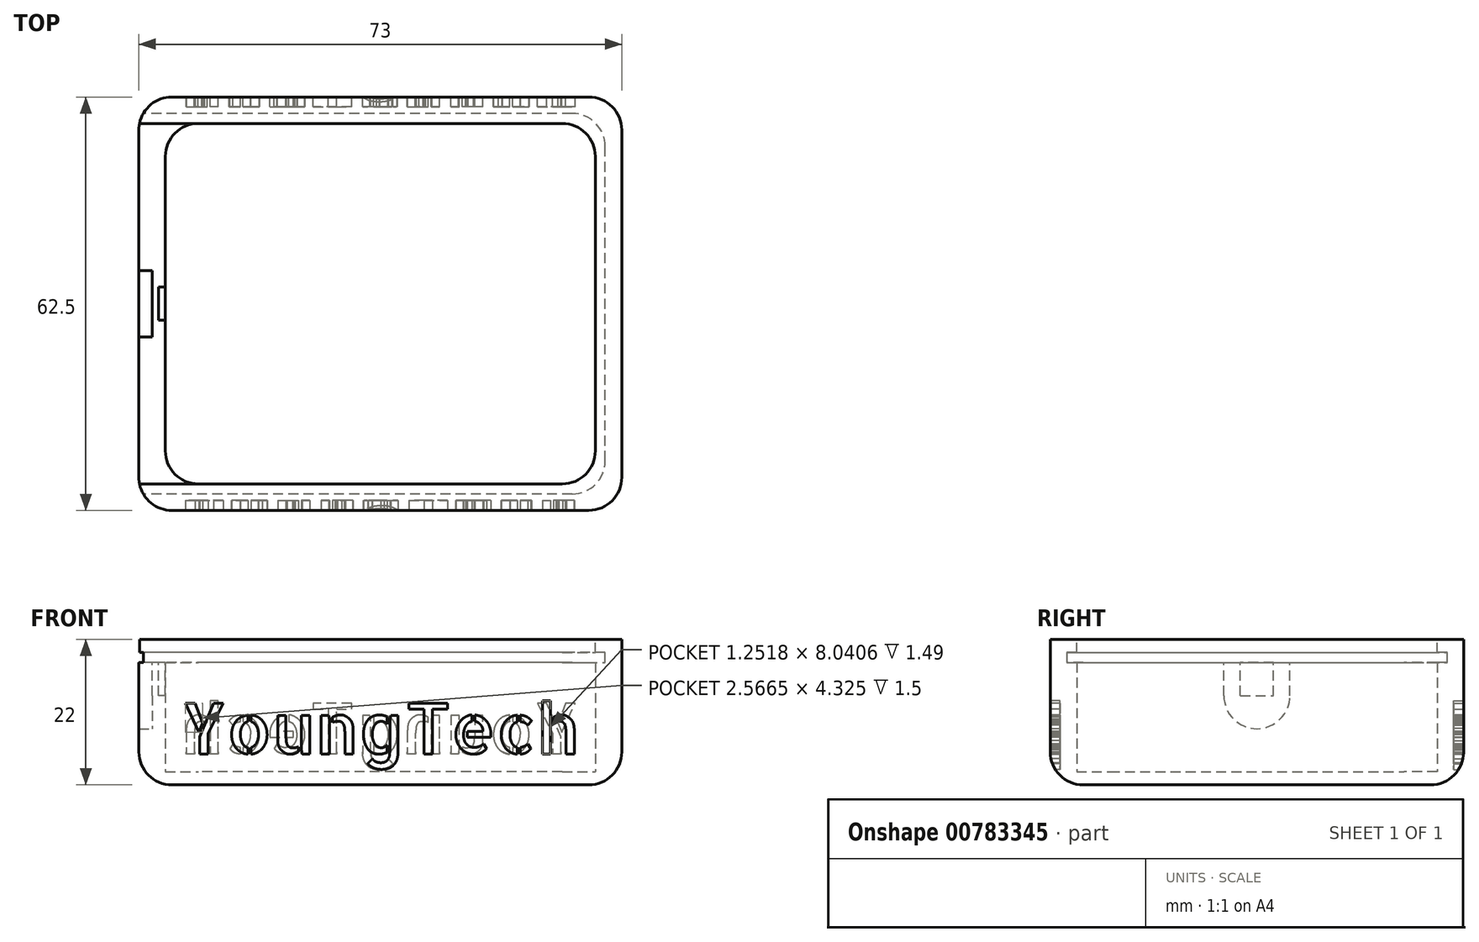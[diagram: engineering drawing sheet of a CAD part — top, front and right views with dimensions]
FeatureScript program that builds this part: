
annotation { "Feature Type Name" : "Feature", "Feature Type Description" : "" }
export const myFeature = defineFeature(function(context is Context, id is Id, definition is map)
    precondition{}
    {
        {
            var Q0;
            Q0=qCreatedBy(makeId("Top.planeOp"),FACE);
            var sketch = newSketch(context, id + "F0", { "sketchPlane" : qUnion([Q0])});
            skLineSegment(sketch, "E0.bottom", {"start": v(36.5, -31.25) * mm, "end": v(-36.5, -31.25) * mm});
            skLineSegment(sketch, "E0.top", {"start": v(36.5, 31.25) * mm, "end": v(-36.5, 31.25) * mm});
            skLineSegment(sketch, "E0.left", {"start": v(36.5, -31.25) * mm, "end": v(36.5, 31.25) * mm});
            skLineSegment(sketch, "E0.right", {"start": v(-36.5, -31.25) * mm, "end": v(-36.5, 31.25) * mm});
            skPoint(sketch, "E0.middle", {"position": v(0, 0) * mm});
            skSolve(sketch);
        }
        {
            var Q0;
            Q0=qSketchRegion(id+"F0",true);
            extrude(context, id + "F1", {"entities" : qUnion([Q0]), "depth" : 2 * mm, "offsetDistance" : 25 * mm});
        }
        {
            var Q0;
            Q0=makeQuery(id+"F1.opExtrude","CAP_FACE",FACE,{"disambiguationData":[OSD([sQuery(id+"F0.wireOp",EDGE,"E0.bottom"),sQuery(id+"F0.wireOp",EDGE,"E0.top"),sQuery(id+"F0.wireOp",EDGE,"E0.left"),sQuery(id+"F0.wireOp",EDGE,"E0.right")])],"isStart":false});
            var sketch = newSketch(context, id + "F2", { "sketchPlane" : qUnion([Q0])});
            skLineSegment(sketch, "E1.0.0", {"start": v(36.5, 31.25) * mm, "end": v(36.5, -31.25) * mm});
            skLineSegment(sketch, "E1.0.1", {"start": v(36.5, -31.25) * mm, "end": v(-36.5, -31.25) * mm});
            skLineSegment(sketch, "E1.0.2", {"start": v(-36.5, -31.25) * mm, "end": v(-36.5, 31.25) * mm});
            skLineSegment(sketch, "E1.0.3", {"start": v(-36.5, 31.25) * mm, "end": v(36.5, 31.25) * mm});
            skLineSegment(sketch, "E2.bottom", {"start": v(32.5, -27.25) * mm, "end": v(-32.5, -27.25) * mm});
            skLineSegment(sketch, "E2.top", {"start": v(32.5, 27.25) * mm, "end": v(-32.5, 27.25) * mm});
            skLineSegment(sketch, "E2.left", {"start": v(32.5, -27.25) * mm, "end": v(32.5, 27.25) * mm});
            skLineSegment(sketch, "E2.right", {"start": v(-32.5, -27.25) * mm, "end": v(-32.5, 27.25) * mm});
            skPoint(sketch, "E2.middle", {"position": v(0, 0) * mm});
            skSolve(sketch);
        }
        {
            var Q0;
            Q0=makeQuery(id+"F2.imprint","IMPRINT",FACE,{"disambiguationData":[TD([[makeQuery(id+"F2.imprint","IMPRINT",EDGE,{"derivedFrom":sQuery(id+"F2.wireOp",EDGE,"E1.0.0")}),1.0]])]});
            extrude(context, id + "F3", {"entities" : qUnion([Q0]), "operationType" : NewBodyOperationType.ADD, "depth" : 20 * mm, "offsetDistance" : 25 * mm});
        }
        {
            var Q0;
            Q0=makeQuery(id+"F3.boolean.opBoolean","MERGE",EDGE,{"derivedFrom":[makeQuery(id+"F1.opExtrude","SWEPT_EDGE",EDGE,{"disambiguationData":[OSD([sQuery(id+"F0.wireOp",EDGE,"E0.top"),sQuery(id+"F0.wireOp",EDGE,"E0.right")])]}),makeQuery(id+"F3.opExtrude","SWEPT_EDGE",EDGE,{"disambiguationData":[OSD([sQuery(id+"F2.wireOp",EDGE,"E1.0.2"),sQuery(id+"F2.wireOp",EDGE,"E1.0.3")])]})]});
            var Q1;
            Q1=makeQuery(id+"F3.boolean.opBoolean","MERGE",EDGE,{"derivedFrom":[makeQuery(id+"F1.opExtrude","SWEPT_EDGE",EDGE,{"disambiguationData":[OSD([sQuery(id+"F0.wireOp",EDGE,"E0.bottom"),sQuery(id+"F0.wireOp",EDGE,"E0.right")])]}),makeQuery(id+"F3.opExtrude","SWEPT_EDGE",EDGE,{"disambiguationData":[OSD([sQuery(id+"F2.wireOp",EDGE,"E1.0.1"),sQuery(id+"F2.wireOp",EDGE,"E1.0.2")])]})]});
            var Q2;
            Q2=makeQuery(id+"F3.boolean.opBoolean","MERGE",EDGE,{"derivedFrom":[makeQuery(id+"F1.opExtrude","SWEPT_EDGE",EDGE,{"disambiguationData":[OSD([sQuery(id+"F0.wireOp",EDGE,"E0.bottom"),sQuery(id+"F0.wireOp",EDGE,"E0.left")])]}),makeQuery(id+"F3.opExtrude","SWEPT_EDGE",EDGE,{"disambiguationData":[OSD([sQuery(id+"F2.wireOp",EDGE,"E1.0.0"),sQuery(id+"F2.wireOp",EDGE,"E1.0.1")])]})]});
            var Q3;
            Q3=makeQuery(id+"F3.opExtrude","SWEPT_EDGE",EDGE,{"disambiguationData":[OSD([sQuery(id+"F2.wireOp",EDGE,"E2.top"),sQuery(id+"F2.wireOp",EDGE,"E2.left")])]});
            var Q4;
            Q4=makeQuery(id+"F3.boolean.opBoolean","MERGE",EDGE,{"derivedFrom":[makeQuery(id+"F1.opExtrude","SWEPT_EDGE",EDGE,{"disambiguationData":[OSD([sQuery(id+"F0.wireOp",EDGE,"E0.top"),sQuery(id+"F0.wireOp",EDGE,"E0.left")])]}),makeQuery(id+"F3.opExtrude","SWEPT_EDGE",EDGE,{"disambiguationData":[OSD([sQuery(id+"F2.wireOp",EDGE,"E1.0.0"),sQuery(id+"F2.wireOp",EDGE,"E1.0.3")])]})]});
            var Q5;
            Q5=makeQuery(id+"F3.opExtrude","SWEPT_EDGE",EDGE,{"disambiguationData":[OSD([sQuery(id+"F2.wireOp",EDGE,"E2.top"),sQuery(id+"F2.wireOp",EDGE,"E2.right")])]});
            var Q6;
            Q6=makeQuery(id+"F3.opExtrude","SWEPT_EDGE",EDGE,{"disambiguationData":[OSD([sQuery(id+"F2.wireOp",EDGE,"E2.bottom"),sQuery(id+"F2.wireOp",EDGE,"E2.right")])]});
            var Q7;
            Q7=makeQuery(id+"F3.opExtrude","SWEPT_EDGE",EDGE,{"disambiguationData":[OSD([sQuery(id+"F2.wireOp",EDGE,"E2.bottom"),sQuery(id+"F2.wireOp",EDGE,"E2.left")])]});
            fillet(context, id + "F4", {"entities" : qUnion([Q0, Q1, Q2, Q3, Q4, Q5, Q6, Q7]), "radius" : 5 * mm, "tangentPropagation" : true, "allowEdgeOverflow" : false});
        }
        {
            var Q0;
            Q0=makeQuery(id+"F3.boolean.opBoolean","MERGE",FACE,{"derivedFrom":[makeQuery(id+"F1.opExtrude","SWEPT_FACE",FACE,{"disambiguationData":[OSD([sQuery(id+"F0.wireOp",EDGE,"E0.right")])]}),makeQuery(id+"F3.opExtrude","SWEPT_FACE",FACE,{"disambiguationData":[OSD([sQuery(id+"F2.wireOp",EDGE,"E1.0.2")])]})]});
            var sketch = newSketch(context, id + "F5", { "sketchPlane" : qUnion([Q0])});
            skLineSegment(sketch, "E3.top", {"start": v(27.25, 22) * mm, "end": v(-27.25, 22) * mm});
            skLineSegment(sketch, "E3.left", {"start": v(27.25, 20) * mm, "end": v(27.25, 22) * mm});
            skLineSegment(sketch, "E3.right", {"start": v(-27.25, 20) * mm, "end": v(-27.25, 22) * mm});
            skLineSegment(sketch, "E4.bottom", {"start": v(28.75, 18.5) * mm, "end": v(-28.75, 18.5) * mm});
            skLineSegment(sketch, "E4.top", {"start": v(28.75, 20) * mm, "end": v(27.25, 20) * mm});
            skLineSegment(sketch, "E4.left", {"start": v(28.75, 18.5) * mm, "end": v(28.75, 20) * mm});
            skLineSegment(sketch, "E4.right", {"start": v(-28.75, 18.5) * mm, "end": v(-28.75, 20) * mm});
            skLineSegment(sketch, "E5.trimOffspring", {"start": v(-27.25, 20) * mm, "end": v(-28.75, 20) * mm});
            skLineSegment(sketch, "E6", {"start": v(0, 22) * mm, "end": v(0, 58.06) * mm, "construction": true});
            skSolve(sketch);
        }
        {
            var Q0;
            Q0=qSketchRegion(id+"F5",true);
            extrude(context, id + "F6", {"entities" : qUnion([Q0]), "operationType" : NewBodyOperationType.REMOVE, "oppositeDirection" : true, "depth" : 69 * mm, "offsetDistance" : 25 * mm});
        }
        {
            var Q0;
            Q0=makeQuery(id+"F6.boolean.opBoolean","COPY",FACE,{"derivedFrom":makeQuery(id+"F6.opExtrude","SWEPT_FACE",FACE,{"disambiguationData":[OSD([sQuery(id+"F5.wireOp",EDGE,"E4.bottom")])]})});
            var sketch = newSketch(context, id + "F7", { "sketchPlane" : qUnion([Q0])});
            skLineSegment(sketch, "E7", {"start": v(0, 0) * mm, "end": v(-32.5, 0) * mm, "construction": true});
            skLineSegment(sketch, "E8.bottom", {"start": v(-32.5, 2.5) * mm, "end": v(-33.5, 2.5) * mm});
            skLineSegment(sketch, "E8.top", {"start": v(-32.5, -2.5) * mm, "end": v(-33.5, -2.5) * mm});
            skLineSegment(sketch, "E8.left", {"start": v(-32.5, 2.5) * mm, "end": v(-32.5, -2.5) * mm});
            skLineSegment(sketch, "E8.right", {"start": v(-33.5, 2.5) * mm, "end": v(-33.5, -2.5) * mm});
            skSolve(sketch);
        }
        {
            var Q0;
            Q0=qSketchRegion(id+"F7",true);
            extrude(context, id + "F8", {"entities" : qUnion([Q0]), "operationType" : NewBodyOperationType.REMOVE, "oppositeDirection" : true, "depth" : 5 * mm, "offsetDistance" : 25 * mm});
        }
        {
            var Q0;
            Q0=makeQuery(id+"F6.boolean.opBoolean","COPY",EDGE,{"derivedFrom":makeQuery(id+"F6.opExtrude","CAP_EDGE",EDGE,{"disambiguationData":[OSD([sQuery(id+"F5.wireOp",EDGE,"E3.left")])],"isStart":false})});
            var Q1;
            Q1=makeQuery(id+"F6.boolean.opBoolean","COPY",EDGE,{"derivedFrom":makeQuery(id+"F6.opExtrude","CAP_EDGE",EDGE,{"disambiguationData":[OSD([sQuery(id+"F5.wireOp",EDGE,"E3.right")])],"isStart":false})});
            fillet(context, id + "F9", {"entities" : qUnion([Q0, Q1]), "radius" : 5 * mm, "tangentPropagation" : true, "allowEdgeOverflow" : false});
        }
        {
            var Q0;
            Q0=makeQuery(id+"F6.boolean.opBoolean","MERGE",FACE,{"derivedFrom":[makeQuery(id+"F3.opExtrude","SWEPT_FACE",FACE,{"disambiguationData":[OSD([sQuery(id+"F2.wireOp",EDGE,"E2.left")])]}),makeQuery(id+"F6.opExtrude","CAP_FACE",FACE,{"disambiguationData":[OSD([sQuery(id+"F5.wireOp",EDGE,"E3.top"),sQuery(id+"F5.wireOp",EDGE,"E3.left"),sQuery(id+"F5.wireOp",EDGE,"E3.right"),sQuery(id+"F5.wireOp",EDGE,"E4.bottom"),sQuery(id+"F5.wireOp",EDGE,"E4.top"),sQuery(id+"F5.wireOp",EDGE,"E4.left"),sQuery(id+"F5.wireOp",EDGE,"E4.right"),sQuery(id+"F5.wireOp",EDGE,"E5.trimOffspring")])],"isStart":false})]});
            var sketch = newSketch(context, id + "F10", { "sketchPlane" : qUnion([Q0])});
            skLineSegment(sketch, "E9.0.2", {"start": v(28.75, 20) * mm, "end": v(-28.75, 20) * mm});
            skLineSegment(sketch, "E9.0.3", {"start": v(-28.75, 20) * mm, "end": v(-28.75, 18.5) * mm});
            skLineSegment(sketch, "E9.0.4", {"start": v(-28.75, 18.5) * mm, "end": v(28.75, 18.5) * mm});
            skLineSegment(sketch, "E9.0.9", {"start": v(28.75, 18.5) * mm, "end": v(28.75, 20) * mm});
            skPoint(sketch, "E10.orphan", {"position": v(-22.25, 20) * mm});
            skPoint(sketch, "E11.orphan", {"position": v(-22.25, 18.5) * mm});
            skSolve(sketch);
        }
        {
            var Q0;
            Q0=qSketchRegion(id+"F10",true);
            extrude(context, id + "F11", {"entities" : qUnion([Q0]), "operationType" : NewBodyOperationType.REMOVE, "oppositeDirection" : true, "depth" : 1.5 * mm, "offsetDistance" : 25 * mm});
        }
        {
            var Q0;
            Q0=makeQuery(id+"F11.boolean.opBoolean","COPY",EDGE,{"derivedFrom":makeQuery(id+"F11.opExtrude","CAP_EDGE",EDGE,{"disambiguationData":[OSD([sQuery(id+"F10.wireOp",EDGE,"E9.0.9")])],"isStart":false})});
            var Q1;
            Q1=makeQuery(id+"F11.boolean.opBoolean","COPY",EDGE,{"derivedFrom":makeQuery(id+"F11.opExtrude","CAP_EDGE",EDGE,{"disambiguationData":[OSD([sQuery(id+"F10.wireOp",EDGE,"E9.0.3")])],"isStart":false})});
            fillet(context, id + "F12", {"entities" : qUnion([Q0, Q1]), "radius" : 5 * mm, "tangentPropagation" : true, "allowEdgeOverflow" : false});
        }
        {
            var Q0;
            Q0=makeQuery(id+"F3.boolean.opBoolean","MERGE",FACE,{"derivedFrom":[makeQuery(id+"F1.opExtrude","SWEPT_FACE",FACE,{"disambiguationData":[OSD([sQuery(id+"F0.wireOp",EDGE,"E0.top")])]}),makeQuery(id+"F3.opExtrude","SWEPT_FACE",FACE,{"disambiguationData":[OSD([sQuery(id+"F2.wireOp",EDGE,"E1.0.3")])]})]});
            var sketch = newSketch(context, id + "F13", { "sketchPlane" : qUnion([Q0])});
            skText(sketch, "E12", { "text": "YoungTech", "fontName": "AllertaStencil-Regular.ttf"});
            skLineSegment(sketch, "E13", {"start": v(-31.5, 0) * mm, "end": v(31.5, 22) * mm, "construction": true});
            skLineSegment(sketch, "E14", {"start": v(-31.5, 11) * mm, "end": v(31.5, 11) * mm, "construction": true});
            const initialGuessF13  = {"E12": [-0.03, 0.00469, 1, 0, 0.00763]};
            skSetInitialGuess(sketch, initialGuessF13);
            skSolve(sketch);
        }
        {
            var Q0;
            Q0=qSketchRegion(id+"F13",true);
            extrude(context, id + "F14", {"entities" : qUnion([Q0]), "operationType" : NewBodyOperationType.REMOVE, "oppositeDirection" : true, "depth" : 1.5 * mm, "offsetDistance" : 25 * mm});
        }
        {
            var Q0;
            Q0=makeQuery(id+"F3.boolean.opBoolean","MERGE",FACE,{"derivedFrom":[makeQuery(id+"F1.opExtrude","SWEPT_FACE",FACE,{"disambiguationData":[OSD([sQuery(id+"F0.wireOp",EDGE,"E0.bottom")])]}),makeQuery(id+"F3.opExtrude","SWEPT_FACE",FACE,{"disambiguationData":[OSD([sQuery(id+"F2.wireOp",EDGE,"E1.0.1")])]})]});
            var sketch = newSketch(context, id + "F15", { "sketchPlane" : qUnion([Q0])});
            skText(sketch, "E15", { "text": "YoungTech", "fontName": "AllertaStencil-Regular.ttf"});
            skLineSegment(sketch, "E16", {"start": v(-31.5, 22) * mm, "end": v(31.5, 0) * mm, "construction": true});
            const initialGuessF15  = {"E15": [-0.03, 0.00469, 1, 0, 0.00763]};
            skSetInitialGuess(sketch, initialGuessF15);
            skSolve(sketch);
        }
        {
            var Q0;
            Q0=qSketchRegion(id+"F15",true);
            extrude(context, id + "F16", {"entities" : qUnion([Q0]), "operationType" : NewBodyOperationType.REMOVE, "oppositeDirection" : true, "depth" : 1.5 * mm, "offsetDistance" : 25 * mm});
        }
        {
            var Q0;
            Q0=makeQuery(id+"F1.opExtrude","CAP_EDGE",EDGE,{"disambiguationData":[OSD([sQuery(id+"F0.wireOp",EDGE,"E0.bottom")])],"isStart":true});
            fillet(context, id + "F17", {"entities" : qUnion([Q0]), "radius" : 5 * mm, "tangentPropagation" : true, "allowEdgeOverflow" : false});
        }
        {
            var Q0;
            Q0=makeQuery(id+"F3.boolean.opBoolean","MERGE",FACE,{"derivedFrom":[makeQuery(id+"F1.opExtrude","SWEPT_FACE",FACE,{"disambiguationData":[OSD([sQuery(id+"F0.wireOp",EDGE,"E0.right")])]}),makeQuery(id+"F3.opExtrude","SWEPT_FACE",FACE,{"disambiguationData":[OSD([sQuery(id+"F2.wireOp",EDGE,"E1.0.2")])]})]});
            var sketch = newSketch(context, id + "F18", { "sketchPlane" : qUnion([Q0])});
            skLineSegment(sketch, "E17.bottom", {"start": v(5, 8.5) * mm, "end": v(-5, 8.5) * mm});
            skLineSegment(sketch, "E17.top", {"start": v(5, 18.5) * mm, "end": v(-5, 18.5) * mm});
            skLineSegment(sketch, "E17.left", {"start": v(5, 8.5) * mm, "end": v(5, 18.5) * mm});
            skLineSegment(sketch, "E17.right", {"start": v(-5, 8.5) * mm, "end": v(-5, 18.5) * mm});
            skPoint(sketch, "E17.middle", {"position": v(0, 13.5) * mm});
            skSolve(sketch);
        }
        {
            var Q0;
            Q0=qSketchRegion(id+"F18",true);
            extrude(context, id + "F19", {"entities" : qUnion([Q0]), "operationType" : NewBodyOperationType.REMOVE, "oppositeDirection" : true, "depth" : 2 * mm, "offsetDistance" : 25 * mm});
        }
        {
            var Q0;
            Q0=makeQuery(id+"F19.boolean.opBoolean","COPY",EDGE,{"derivedFrom":makeQuery(id+"F19.opExtrude","SWEPT_EDGE",EDGE,{"disambiguationData":[OSD([sQuery(id+"F18.wireOp",EDGE,"E17.bottom"),sQuery(id+"F18.wireOp",EDGE,"E17.right")])]})});
            var Q1;
            Q1=makeQuery(id+"F19.boolean.opBoolean","COPY",EDGE,{"derivedFrom":makeQuery(id+"F19.opExtrude","SWEPT_EDGE",EDGE,{"disambiguationData":[OSD([sQuery(id+"F18.wireOp",EDGE,"E17.bottom"),sQuery(id+"F18.wireOp",EDGE,"E17.left")])]})});
            var Q2;
            Q2=makeQuery(id+"F19.boolean.opBoolean","COPY",EDGE,{"derivedFrom":makeQuery(id+"F19.opExtrude","SWEPT_EDGE",EDGE,{"disambiguationData":[OSD([sQuery(id+"F5.wireOp",EDGE,"E4.bottom"),sQuery(id+"F18.wireOp",EDGE,"E17.top"),sQuery(id+"F18.wireOp",EDGE,"E17.left")])]})});
            var Q3;
            Q3=makeQuery(id+"F19.boolean.opBoolean","COPY",EDGE,{"derivedFrom":makeQuery(id+"F19.opExtrude","SWEPT_EDGE",EDGE,{"disambiguationData":[OSD([sQuery(id+"F5.wireOp",EDGE,"E4.bottom"),sQuery(id+"F18.wireOp",EDGE,"E17.top"),sQuery(id+"F18.wireOp",EDGE,"E17.right")])]})});
            fillet(context, id + "F20", {"entities" : qUnion([Q0, Q1, Q2, Q3]), "radius" : 5 * mm, "tangentPropagation" : true, "allowEdgeOverflow" : false});
        }
    });
